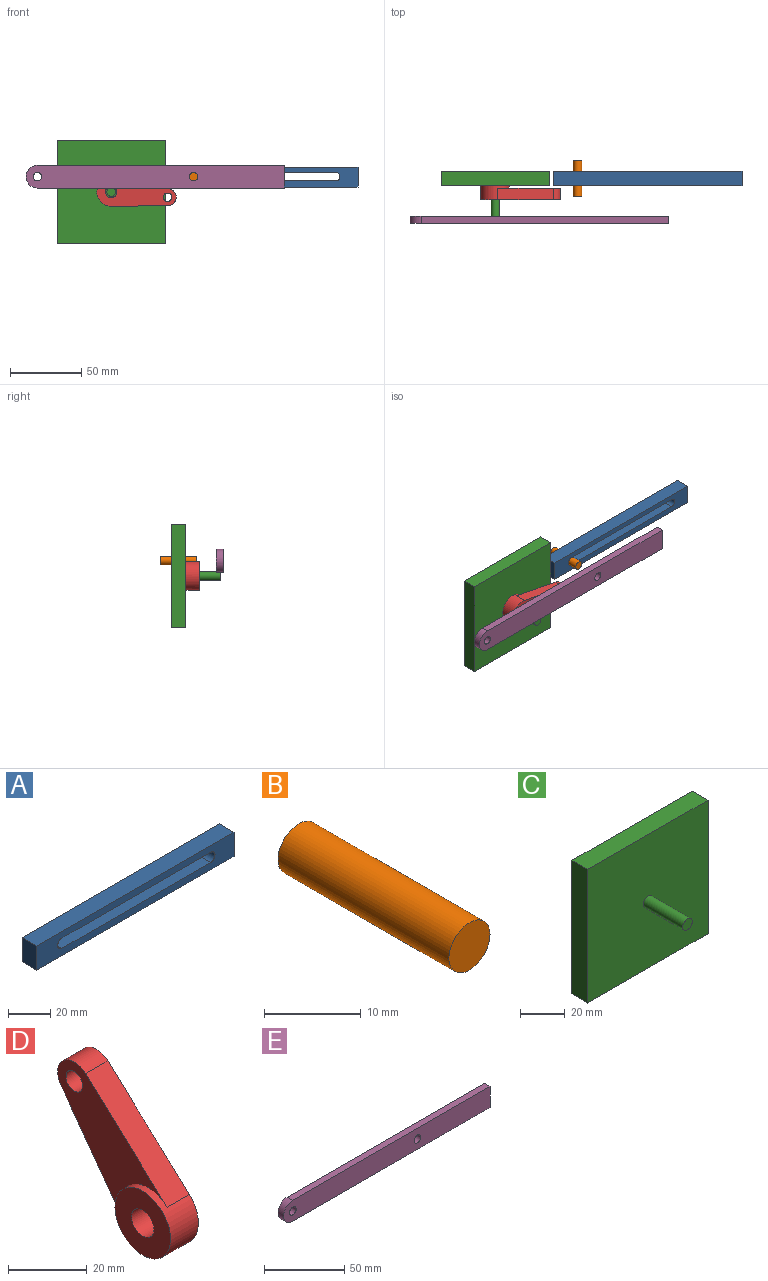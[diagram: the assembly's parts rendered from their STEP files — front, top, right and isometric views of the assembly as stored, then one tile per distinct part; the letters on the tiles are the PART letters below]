
ASSEMBLY  parts=5 mates=3
PART A: 10 faces, bbox 132.7x10x14 mm
  f0: plane 14.02x10mm, normal (-1,0,0), area 140.2mm2, adj f1,f7,f8,f9
  f1: plane 132.66x10mm, normal (0,0,-1), area 1326.6mm2, adj f0,f2,f8,f9
  f2: plane 14.02x10mm, normal (1,0,0), area 140.2mm2, adj f1,f7,f8,f9
  f3: cylinder r=3mm len=10mm, axis (0,1,0), area 94.2mm2, adj f4,f6,f8,f9
  f4: plane 100x10mm, normal (0,0,1), area 1000mm2, adj f3,f5,f8,f9
  f5: cylinder r=3mm len=10mm, axis (0,1,0), area 94.2mm2, adj f4,f6,f8,f9
  f6: plane 100x10mm, normal (0,0,-1), area 1000mm2, adj f3,f5,f8,f9
  f7: plane 132.66x10mm, normal (0,0,1), area 1326.6mm2, adj f0,f2,f8,f9
  f8: plane 132.66x14.02mm, normal (0,-1,0), area 1232.1mm2, adj f0,f1,f2,f3,f4,f5,f6,f7
  f9: plane 132.66x14.02mm, normal (0,1,0), area 1232.1mm2, adj f0,f1,f2,f3,f4,f5,f6,f7
PART B: 3 faces, bbox 6x25x6 mm
  f0: cylinder r=3mm len=25mm, axis (0,1,0), area 471.2mm2, adj f1,f2
  f1: plane 6x6mm, normal (0,-1,0), area 28.3mm2, adj f0
  f2: plane 6x6mm, normal (0,1,0), area 28.3mm2, adj f0
PART C: 8 faces, bbox 76.1x35x73.1 mm
  f0: plane 73.11x10mm, normal (1,0,0), area 731.1mm2, adj f1,f3,f4,f5
  f1: plane 76.07x10mm, normal (0,0,1), area 760.7mm2, adj f0,f2,f4,f5
  f2: plane 73.11x10mm, normal (-1,0,0), area 731.1mm2, adj f1,f3,f4,f5
  f3: plane 76.07x10mm, normal (0,0,-1), area 760.7mm2, adj f0,f2,f4,f5
  f4: plane 76.07x73.11mm, normal (0,-1,0), area 5533.2mm2, adj f0,f1,f2,f3,f6
  f5: plane 76.07x73.11mm, normal (0,1,0), area 5561.5mm2, adj f0,f1,f2,f3
  f6: cylinder r=3mm len=25mm, axis (0,1,0), area 471.2mm2, adj f4,f7
  f7: plane 6x6mm, normal (0,-1,0), area 28.3mm2, adj f6
PART D: 9 faces, bbox 10x42.6x45.9 mm
  f0: plane 32.21x23.38mm, normal (0,0.81,-0.59), area 318.4mm2, adj f1,f5,f6,f7
  f1: cylinder r=6mm len=10.06mm, axis (-1,0,0), area 141.2mm2, adj f0,f2,f6,f7
  f2: plane 29.32x26.91mm, normal (0,-0.68,0.74), area 318.4mm2, adj f1,f5,f6,f7
  f3: cylinder r=4mm len=10mm, axis (-1,0,0), area 251.3mm2, adj f6,f8
  f4: cylinder r=3mm len=8mm, axis (-1,0,0), area 150.8mm2, adj f6,f7
  f5: cylinder r=10mm len=20mm, axis (-1,0,0), area 393mm2, adj f0,f2,f6,f7,f8
  f6: plane 45.86x42.62mm, normal (1,0,0), area 778.3mm2, adj f0,f1,f2,f3,f4,f5
  f7: plane 41.73x39.38mm, normal (-1,0,0), area 514.4mm2, adj f0,f1,f2,f4,f5
  f8: plane 20x20mm, normal (-1,0,0), area 263.9mm2, adj f3,f5
PART E: 8 faces, bbox 181.9x5x16 mm
  f0: plane 16x5mm, normal (1,0,0), area 80mm2, adj f1,f5,f6,f7
  f1: plane 173.95x5mm, normal (0,0,1), area 869.7mm2, adj f0,f2,f6,f7
  f2: cylinder r=8mm len=16mm, axis (0,1,0), area 125.7mm2, adj f1,f5,f6,f7
  f3: cylinder r=3mm len=6mm, axis (0,1,0), area 94.2mm2, adj f6,f7
  f4: cylinder r=3mm len=6mm, axis (0,1,0), area 94.2mm2, adj f6,f7
  f5: plane 173.95x5mm, normal (0,0,-1), area 869.7mm2, adj f0,f2,f6,f7
  f6: plane 181.95x16mm, normal (0,-1,0), area 2827.2mm2, adj f0,f1,f2,f3,f4,f5
  f7: plane 181.95x16mm, normal (0,1,0), area 2827.2mm2, adj f0,f1,f2,f3,f4,f5
PLACE A t=(241.69,5.55,-12.05)mm fixed
PLACE B rot(axis=(-1,0,0),180deg) t=(68.42,-11.95,27.03)mm
PLACE C t=(-8.15,5.79,-10.5)mm fixed
PLACE D rot(axis=(-0.41,0.41,-0.81),101.7deg) t=(-8.15,-6.21,-10.5)mm
PLACE E rot(axis=(0,-1,0),0deg) t=(-35.09,-25.93,57.45)mm
MATE cylindrical B.f0 <-> E.f4  axis (0,-1,0) through (49.93,0.55,0.28)mm
MATE pin_slot A.f5 <-> B.f0  axis (0,1,0) through (49.93,0.55,0.28)mm
MATE revolute C.f6 <-> D.f3  axis (0,1,0) through (-8.15,-4.21,-10.5)mm
